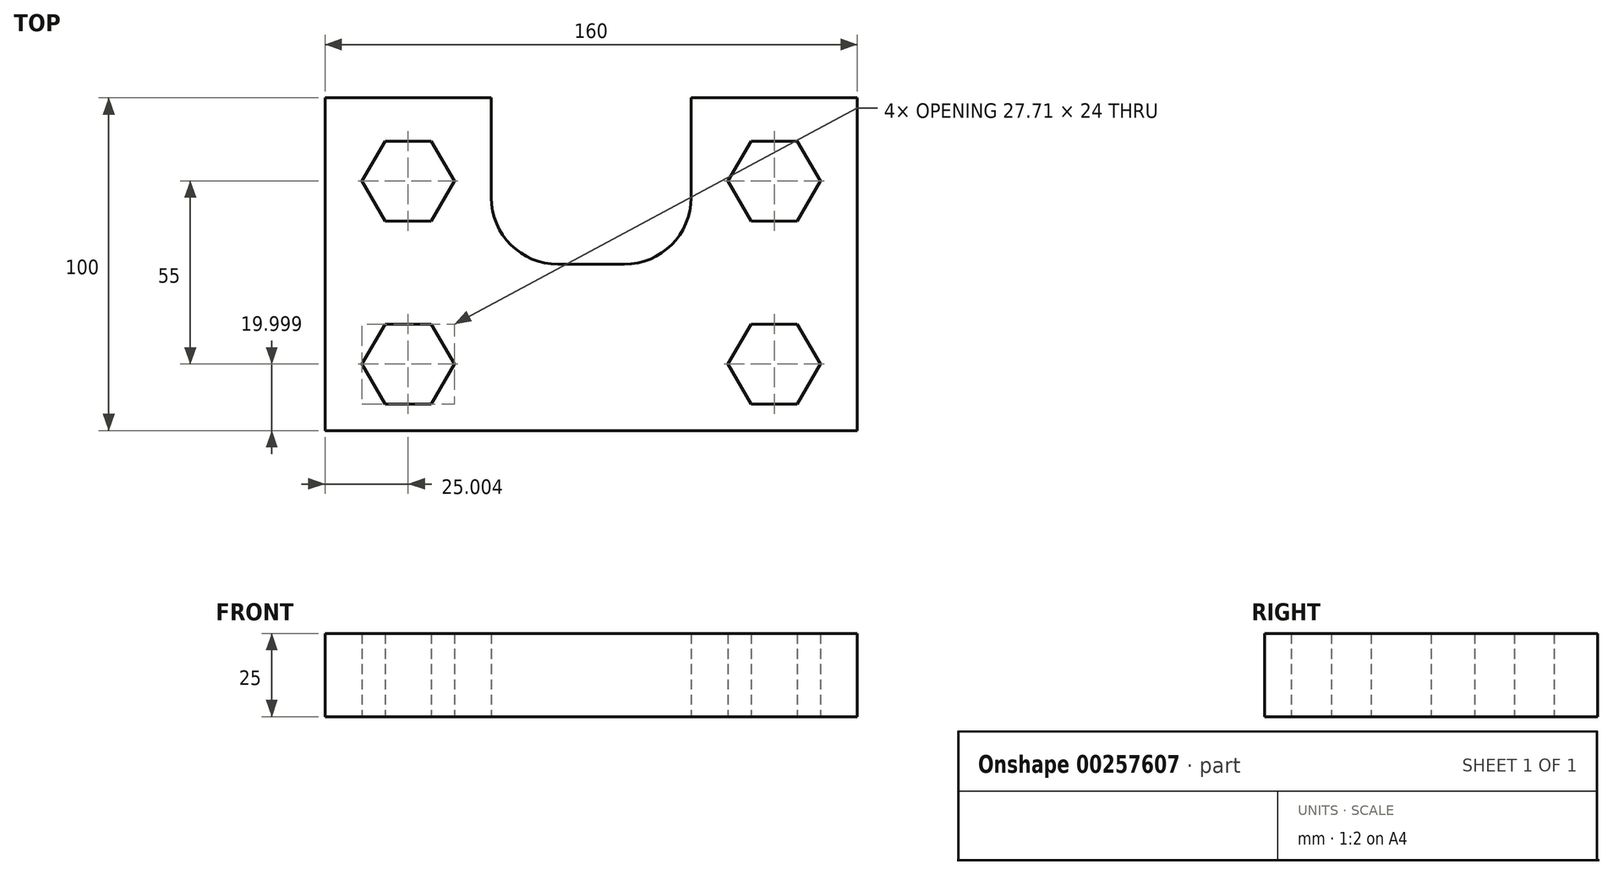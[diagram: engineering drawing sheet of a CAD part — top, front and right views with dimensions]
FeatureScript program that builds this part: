
annotation { "Feature Type Name" : "Feature", "Feature Type Description" : "" }
export const myFeature = defineFeature(function(context is Context, id is Id, definition is map)
    precondition{}
    {
        {
            var Q0;
            Q0=qCreatedBy(makeId("Top.planeOp"),FACE);
            var sketch = newSketch(context, id + "F0", { "sketchPlane" : qUnion([Q0])});
            skLineSegment(sketch, "E0", {"start": v(-99.25, -108) * mm, "end": v(60.75, -108) * mm});
            skLineSegment(sketch, "E1", {"start": v(60.75, -108) * mm, "end": v(60.75, -8) * mm});
            skLineSegment(sketch, "E2", {"start": v(60.75, -8) * mm, "end": v(10.75, -8) * mm});
            skLineSegment(sketch, "E3", {"start": v(10.75, -8) * mm, "end": v(10.75, -38) * mm});
            skLineSegment(sketch, "E4", {"start": v(-9.25, -58) * mm, "end": v(-29.25, -58) * mm});
            skLineSegment(sketch, "E5", {"start": v(-49.25, -38) * mm, "end": v(-49.25, -8) * mm});
            skLineSegment(sketch, "E6", {"start": v(-49.25, -8) * mm, "end": v(-99.25, -8) * mm});
            skLineSegment(sketch, "E7", {"start": v(-99.25, -8) * mm, "end": v(-99.25, -108) * mm});
            skCircle(sketch, "E8.cCircle", {"center": v(35.75, -33) * mm, "radius": 12 * mm, "construction": true});
            skLineSegment(sketch, "E8.0", {"start": v(42.68, -45) * mm, "end": v(28.83, -45) * mm});
            skLineSegment(sketch, "E8.1", {"start": v(28.83, -45) * mm, "end": v(21.9, -33) * mm});
            skLineSegment(sketch, "E8.2", {"start": v(21.9, -33) * mm, "end": v(28.83, -21) * mm});
            skLineSegment(sketch, "E8.3", {"start": v(28.83, -21) * mm, "end": v(42.68, -21) * mm});
            skLineSegment(sketch, "E8.4", {"start": v(42.68, -21) * mm, "end": v(49.61, -33) * mm});
            skLineSegment(sketch, "E8.5", {"start": v(49.61, -33) * mm, "end": v(42.68, -45) * mm});
            skPoint(sketch, "E8.0.midPoint", {"position": v(35.75, -45) * mm});
            skCircle(sketch, "E9.cCircle", {"center": v(-74.25, -33) * mm, "radius": 12 * mm, "construction": true});
            skLineSegment(sketch, "E9.0", {"start": v(-81.17, -21) * mm, "end": v(-67.32, -21) * mm});
            skLineSegment(sketch, "E9.1", {"start": v(-67.32, -21) * mm, "end": v(-60.39, -33) * mm});
            skLineSegment(sketch, "E9.2", {"start": v(-60.39, -33) * mm, "end": v(-67.32, -45) * mm});
            skLineSegment(sketch, "E9.3", {"start": v(-67.32, -45) * mm, "end": v(-81.17, -45) * mm});
            skLineSegment(sketch, "E9.4", {"start": v(-81.17, -45) * mm, "end": v(-88.1, -33) * mm});
            skLineSegment(sketch, "E9.5", {"start": v(-88.1, -33) * mm, "end": v(-81.17, -21) * mm});
            skPoint(sketch, "E9.0.midPoint", {"position": v(-74.25, -21) * mm});
            skCircle(sketch, "E10.cCircle", {"center": v(-74.25, -88) * mm, "radius": 12 * mm, "construction": true});
            skLineSegment(sketch, "E10.0", {"start": v(-81.17, -76) * mm, "end": v(-67.32, -76) * mm});
            skLineSegment(sketch, "E10.1", {"start": v(-67.32, -76) * mm, "end": v(-60.39, -88) * mm});
            skLineSegment(sketch, "E10.2", {"start": v(-60.39, -88) * mm, "end": v(-67.32, -100) * mm});
            skLineSegment(sketch, "E10.3", {"start": v(-67.32, -100) * mm, "end": v(-81.17, -100) * mm});
            skLineSegment(sketch, "E10.4", {"start": v(-81.17, -100) * mm, "end": v(-88.1, -88) * mm});
            skLineSegment(sketch, "E10.5", {"start": v(-88.1, -88) * mm, "end": v(-81.17, -76) * mm});
            skPoint(sketch, "E10.0.midPoint", {"position": v(-74.25, -76) * mm});
            skCircle(sketch, "E11.cCircle", {"center": v(35.75, -88) * mm, "radius": 12 * mm, "construction": true});
            skLineSegment(sketch, "E11.0", {"start": v(28.83, -76) * mm, "end": v(42.68, -76) * mm});
            skLineSegment(sketch, "E11.1", {"start": v(42.68, -76) * mm, "end": v(49.61, -88) * mm});
            skLineSegment(sketch, "E11.2", {"start": v(49.61, -88) * mm, "end": v(42.68, -100) * mm});
            skLineSegment(sketch, "E11.3", {"start": v(42.68, -100) * mm, "end": v(28.83, -100) * mm});
            skLineSegment(sketch, "E11.4", {"start": v(28.83, -100) * mm, "end": v(21.9, -88) * mm});
            skLineSegment(sketch, "E11.5", {"start": v(21.9, -88) * mm, "end": v(28.83, -76) * mm});
            skPoint(sketch, "E11.0.midPoint", {"position": v(35.75, -76) * mm});
            skPoint(sketch, "E12.visualSharp", {"position": v(-49.25, -58) * mm});
            skArc(sketch, "E12.filletArc", {"start": v(-49.25, -38) * mm, "mid": v(-43.39, -52.14) * mm, "end": v(-29.25, -58) * mm});
            skPoint(sketch, "E13.visualSharp", {"position": v(10.75, -58) * mm});
            skArc(sketch, "E13.filletArc", {"start": v(-9.25, -58) * mm, "mid": v(4.9, -52.14) * mm, "end": v(10.75, -38) * mm});
            skSolve(sketch);
        }
        {
            var Q0;
            Q0=makeQuery(id+"F0.imprint","IMPRINT",FACE,{"disambiguationData":[TD([[makeQuery(id+"F0.imprint","IMPRINT",EDGE,{"derivedFrom":sQuery(id+"F0.wireOp",EDGE,"E0")}),1.0]])]});
            extrude(context, id + "F1", {"entities" : qUnion([Q0]), "depth" : 25 * mm});
        }
    });
